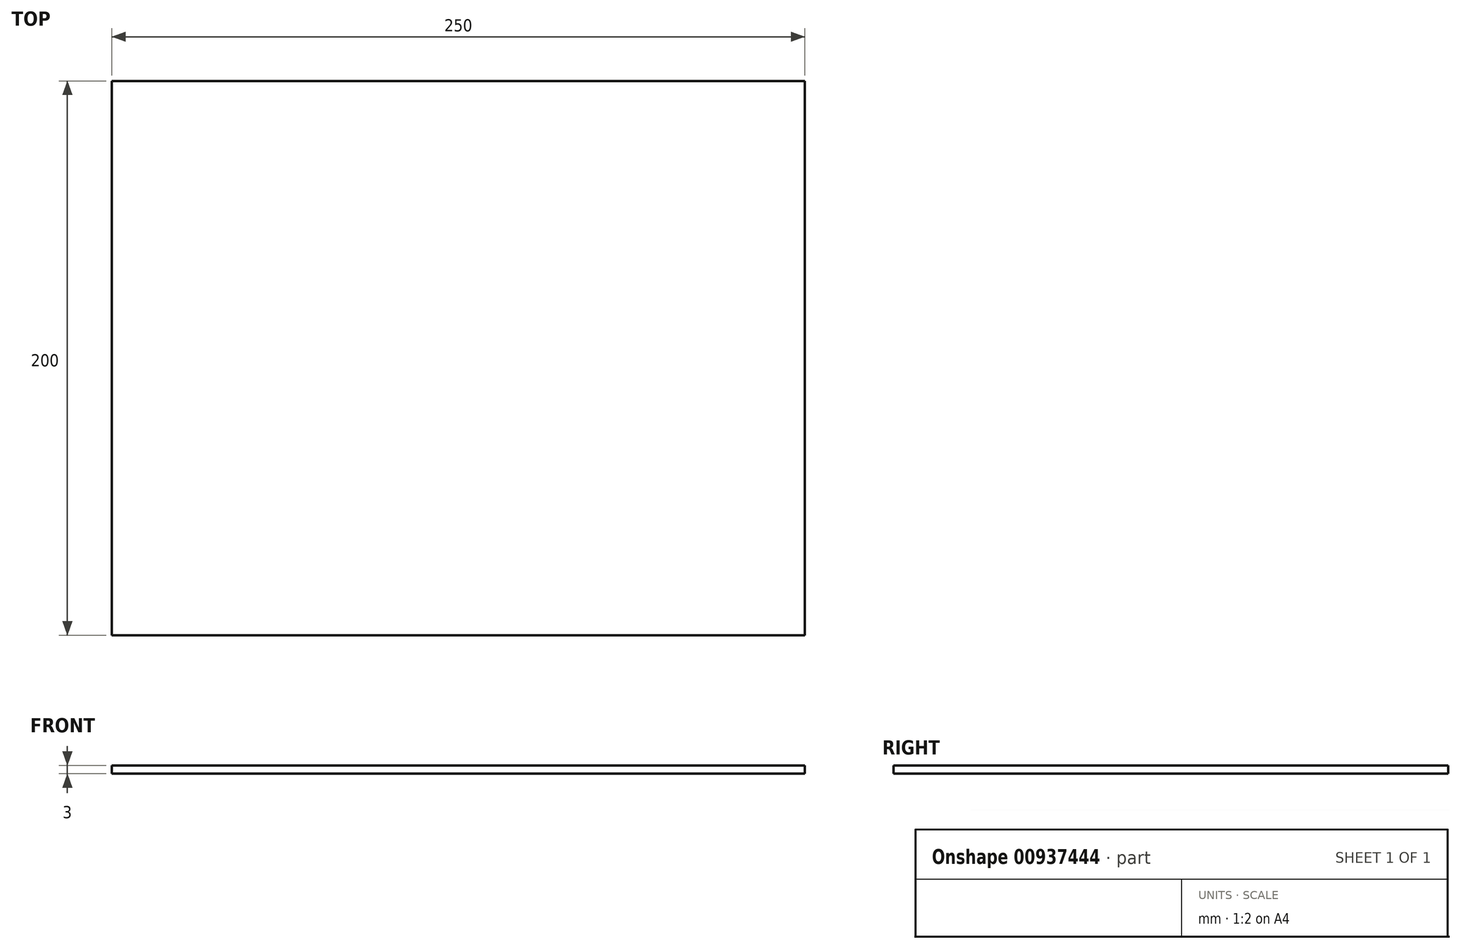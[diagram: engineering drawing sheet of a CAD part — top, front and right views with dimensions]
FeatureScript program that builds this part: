
annotation { "Feature Type Name" : "Feature", "Feature Type Description" : "" }
export const myFeature = defineFeature(function(context is Context, id is Id, definition is map)
    precondition{}
    {
        {
            var Q0;
            Q0=qCreatedBy(makeId("Top.planeOp"),FACE);
            var sketch = newSketch(context, id + "F0", { "sketchPlane" : qUnion([Q0])});
            skLineSegment(sketch, "E0.bottom", {"start": v(0, 0) * mm, "end": v(250, 0) * mm});
            skLineSegment(sketch, "E0.top", {"start": v(0, 200) * mm, "end": v(250, 200) * mm});
            skLineSegment(sketch, "E0.left", {"start": v(0, 0) * mm, "end": v(0, 200) * mm});
            skLineSegment(sketch, "E0.right", {"start": v(250, 0) * mm, "end": v(250, 200) * mm});
            skSolve(sketch);
        }
        {
            var Q0;
            Q0 = qSketchRegion(id + "F0", true);
            extrude(context, id + "F1", {"entities" : qUnion([Q0]), "depth" : 3 * mm, "offsetDistance" : 25 * mm});
        }
    });
